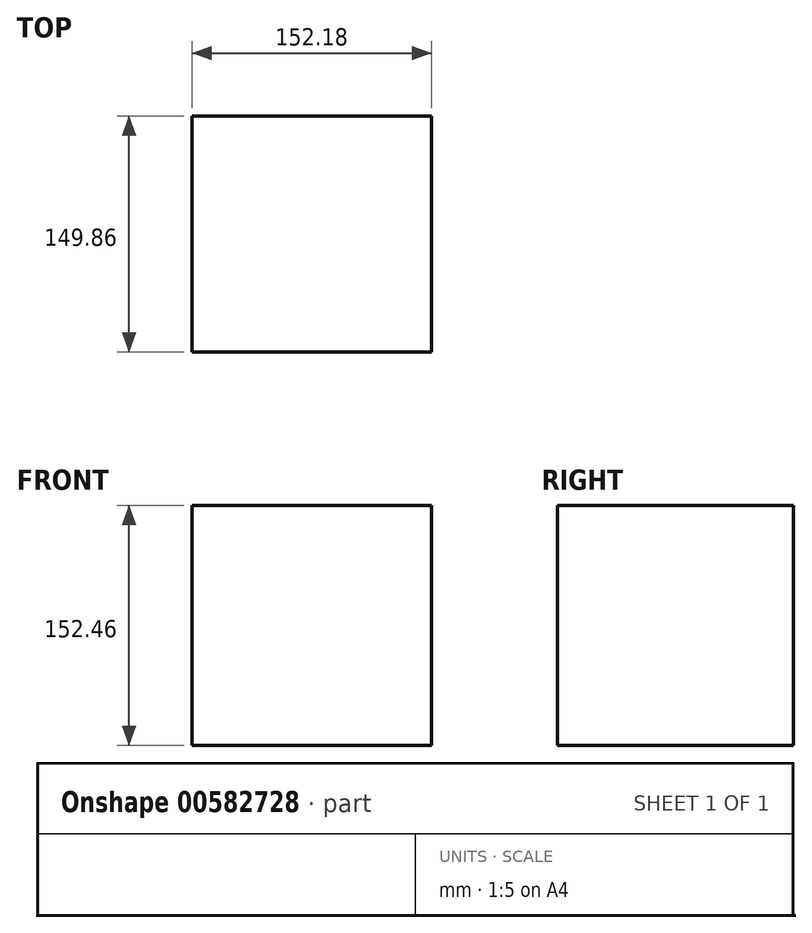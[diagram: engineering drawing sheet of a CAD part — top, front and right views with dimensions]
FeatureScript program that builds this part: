
annotation { "Feature Type Name" : "Feature", "Feature Type Description" : "" }
export const myFeature = defineFeature(function(context is Context, id is Id, definition is map)
    precondition{}
    {
        {
            var Q0;
            Q0=qCreatedBy(makeId("Front.planeOp"),FACE);
            var sketch = newSketch(context, id + "F0", { "sketchPlane" : qUnion([Q0])});
            skLineSegment(sketch, "E0", {"start": v(-76.23, 76.51) * mm, "end": v(-76.23, -75.95) * mm});
            skLineSegment(sketch, "E1", {"start": v(-76.23, -75.95) * mm, "end": v(75.95, -75.95) * mm});
            skLineSegment(sketch, "E2", {"start": v(75.95, -75.95) * mm, "end": v(75.95, 76.51) * mm});
            skLineSegment(sketch, "E3", {"start": v(75.95, 76.51) * mm, "end": v(-76.23, 76.51) * mm});
            skSolve(sketch);
        }
        {
            var Q0;
            Q0=makeQuery(id+"F0.imprint","IMPRINT",FACE,{"disambiguationData":[TD([[makeQuery(id+"F0.imprint","IMPRINT",EDGE,{"derivedFrom":sQuery(id+"F0.wireOp",EDGE,"E0")}),1.0]])]});
            extrude(context, id + "F1", {"entities" : qUnion([Q0]), "depth" : 149.86 * mm, "offsetDistance" : 25.4 * mm});
        }
    });
